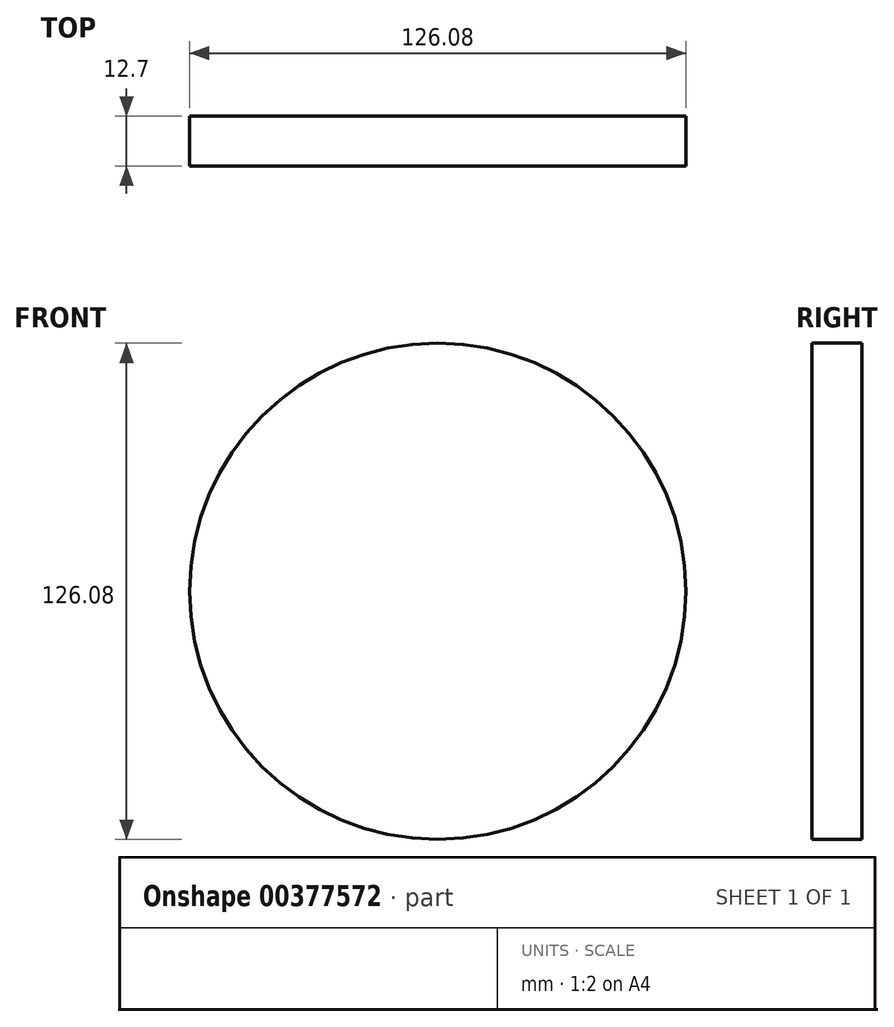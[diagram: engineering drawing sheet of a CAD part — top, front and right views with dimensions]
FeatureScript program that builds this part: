
annotation { "Feature Type Name" : "Feature", "Feature Type Description" : "" }
export const myFeature = defineFeature(function(context is Context, id is Id, definition is map)
    precondition{}
    {
        {
            var Q0;
            Q0=qCreatedBy(makeId("Front.planeOp"),FACE);
            var sketch = newSketch(context, id + "F0", { "sketchPlane" : qUnion([Q0])});
            skCircle(sketch, "E0", {"center": v(0, 0) * mm, "radius": 63.04 * mm});
            skSolve(sketch);
        }
        {
            var Q0;
            Q0=makeQuery(id+"F0.imprint","IMPRINT",FACE,{"disambiguationData":[TD([[makeQuery(id+"F0.imprint","IMPRINT",EDGE,{"derivedFrom":sQuery(id+"F0.wireOp",EDGE,"E0")}),1.0]])]});
            var Q1;
            Q1=sQuery(id+"F0.wireOp",EDGE,"E0");
            extrude(context, id + "F1", {"entities" : qUnion([Q0]), "bodyType" : ToolBodyType.SURFACE, "surfaceEntities" : qUnion([Q1]), "depth" : 25.4 * mm});
        }
        {
            var Q0;
            Q0=makeQuery(id+"F0.imprint","IMPRINT",FACE,{"disambiguationData":[TD([[makeQuery(id+"F0.imprint","IMPRINT",EDGE,{"derivedFrom":sQuery(id+"F0.wireOp",EDGE,"E0")}),1.0]])]});
            extrude(context, id + "F2", {"entities" : qUnion([Q0]), "depth" : 12.7 * mm});
        }
    });
